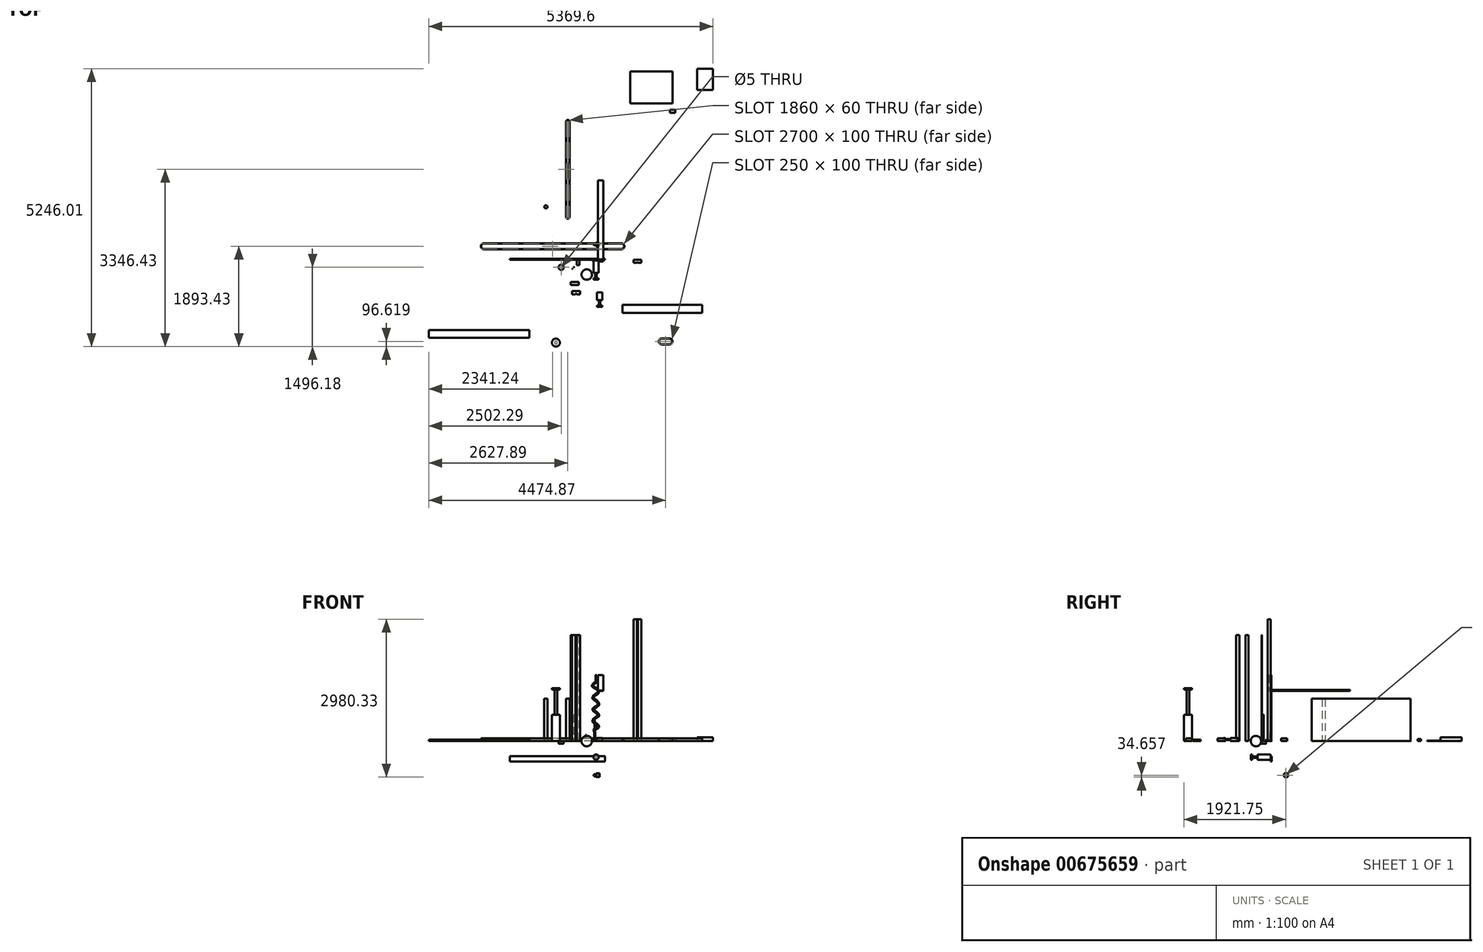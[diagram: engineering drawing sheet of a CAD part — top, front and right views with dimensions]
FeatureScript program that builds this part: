
annotation { "Feature Type Name" : "Feature", "Feature Type Description" : "" }
export const myFeature = defineFeature(function(context is Context, id is Id, definition is map)
    precondition{}
    {
        {
            var Q0;
            Q0=qCreatedBy(makeId("Top.planeOp"),FACE);
            var sketch = newSketch(context, id + "F0", { "sketchPlane" : qUnion([Q0])});
            skCircle(sketch, "E0", {"center": v(-422.62, -169.33) * mm, "radius": 2.5 * mm});
            skSolve(sketch);
        }
        {
            var Q0;
            Q0=makeQuery(id+"F0.imprint","IMPRINT",FACE,{"disambiguationData":[TD([[makeQuery(id+"F0.imprint","IMPRINT",EDGE,{"derivedFrom":sQuery(id+"F0.wireOp",EDGE,"E0")}),1.0]])]});
            extrude(context, id + "F1", {"entities" : qUnion([Q0]), "depth" : 2000 * mm, "offsetDistance" : 25 * mm});
        }
        {
            var Q0;
            Q0=qCreatedBy(makeId("Top.planeOp"),FACE);
            var sketch = newSketch(context, id + "F2", { "sketchPlane" : qUnion([Q0])});
            skCircle(sketch, "E1", {"center": v(-634.46, -142.18) * mm, "radius": 50 * mm});
            skCircle(sketch, "E2", {"center": v(-634.46, -142.18) * mm, "radius": 2.5 * mm});
            skSolve(sketch);
        }
        {
            var Q0;
            Q0=makeQuery(id+"F2.imprint","IMPRINT",FACE,{"disambiguationData":[TD([[makeQuery(id+"F2.imprint","IMPRINT",EDGE,{"derivedFrom":sQuery(id+"F2.wireOp",EDGE,"E1")}),1.0]])]});
            extrude(context, id + "F3", {"entities" : qUnion([Q0]), "oppositeDirection" : true, "depth" : 50 * mm, "offsetDistance" : 25 * mm});
        }
        {
            var Q0;
            Q0=qCreatedBy(makeId("Top.planeOp"),FACE);
            var sketch = newSketch(context, id + "F4", { "sketchPlane" : qUnion([Q0])});
            skLineSegment(sketch, "E3", {"start": v(-97.3, -196.52) * mm, "end": v(-205.2, -361.27) * mm, "construction": true});
            skArc(sketch, "E4", {"start": v(-205.2, -361.27) * mm, "mid": v(-68.88, -332.84) * mm, "end": v(-97.3, -196.52) * mm});
            skLineSegment(sketch, "E5", {"start": v(-205.2, -361.27) * mm, "end": v(-97.3, -196.52) * mm});
            skSolve(sketch);
        }
        {
            var Q0;
            Q0=makeQuery(id+"F4.imprint","IMPRINT",FACE,{"disambiguationData":[TD([[makeQuery(id+"F4.imprint","IMPRINT",EDGE,{"derivedFrom":sQuery(id+"F4.wireOp",EDGE,"E4")}),1.0]])]});
            var Q1;
            Q1=sQuery(id+"F4.wireOp",EDGE,"E4");
            var Q2;
            Q2=sQuery(id+"F4.wireOp",EDGE,"E5");
            revolve(context, id + "F5", {"entities" : qUnion([Q0]), "surfaceEntities" : qUnion([Q1]), "axis" : qUnion([Q2]), "revolveType" : RevolveType.FULL});
        }
        {
            var Q0;
            Q0=qCreatedBy(makeId("Top.planeOp"),FACE);
            var sketch = newSketch(context, id + "F6", { "sketchPlane" : qUnion([Q0])});
            skLineSegment(sketch, "E6.bottom", {"start": v(-2095.5, 305.07) * mm, "end": v(504.5, 305.07) * mm});
            skLineSegment(sketch, "E6.top", {"start": v(-2095.5, 205.07) * mm, "end": v(504.5, 205.07) * mm});
            skArc(sketch, "E7", {"start": v(504.5, 205.07) * mm, "mid": v(554.5, 255.07) * mm, "end": v(504.5, 305.07) * mm});
            skArc(sketch, "E8", {"start": v(-2095.5, 305.07) * mm, "mid": v(-2145.5, 255.07) * mm, "end": v(-2095.5, 205.07) * mm});
            skLineSegment(sketch, "E9.bottom", {"start": v(504.5, 311.07) * mm, "end": v(-2095.5, 311.07) * mm});
            skLineSegment(sketch, "E9.top", {"start": v(504.5, 199.07) * mm, "end": v(-2095.5, 199.07) * mm});
            skLineSegment(sketch, "E9.left", {"start": v(504.5, 311.07) * mm, "end": v(504.5, 199.07) * mm});
            skLineSegment(sketch, "E9.right", {"start": v(-2095.5, 311.07) * mm, "end": v(-2095.5, 199.07) * mm});
            skPoint(sketch, "E9.middle", {"position": v(-795.5, 255.07) * mm});
            skPoint(sketch, "E9.middle.positionSnap0", {"position": v(-795.5, 205.07) * mm});
            skPoint(sketch, "E9.centerSnap0", {"position": v(-795.5, 205.07) * mm});
            skArc(sketch, "E10", {"start": v(504.5, 199.07) * mm, "mid": v(560.5, 255.07) * mm, "end": v(504.5, 311.07) * mm});
            skArc(sketch, "E11", {"start": v(-2095.5, 311.07) * mm, "mid": v(-2151.5, 255.07) * mm, "end": v(-2095.5, 199.07) * mm});
            skSolve(sketch);
        }
        {
            var Q0;
            {var subQ0=sQuery(id+"F6.wireOp",EDGE,"E6.top");Q0=makeQuery(id+"F6.imprint","IMPRINT",FACE,{"disambiguationData":[TD([[makeQuery(id+"F6.imprint","IMPRINT",EDGE,{"derivedFrom":subQ0}),-1.0]])]});}
            var Q1;
            {var subQ0=sQuery(id+"F6.wireOp",EDGE,"E8");Q1=makeQuery(id+"F6.imprint","IMPRINT",FACE,{"disambiguationData":[TD([[makeQuery(id+"F6.imprint","IMPRINT",EDGE,{"derivedFrom":subQ0}),-1.0]])]});}
            var Q2;
            {var subQ0=sQuery(id+"F6.wireOp",EDGE,"E6.bottom");Q2=makeQuery(id+"F6.imprint","IMPRINT",FACE,{"disambiguationData":[TD([[makeQuery(id+"F6.imprint","IMPRINT",EDGE,{"derivedFrom":subQ0}),1.0]])]});}
            var Q3;
            {var subQ0=sQuery(id+"F6.wireOp",EDGE,"E7");Q3=makeQuery(id+"F6.imprint","IMPRINT",FACE,{"disambiguationData":[TD([[makeQuery(id+"F6.imprint","IMPRINT",EDGE,{"derivedFrom":subQ0}),-1.0]])]});}
            extrude(context, id + "F7", {"entities" : qUnion([Q0, Q1, Q2, Q3]), "depth" : 50 * mm, "offsetDistance" : 25 * mm});
        }
        {
            var Q0;
            Q0=qCreatedBy(makeId("Front.planeOp"),FACE);
            var sketch = newSketch(context, id + "F8", { "sketchPlane" : qUnion([Q0])});
            skLineSegment(sketch, "E12.bottom", {"start": v(-172.22, 116.45) * mm, "end": v(-157.22, 116.45) * mm});
            skLineSegment(sketch, "E12.top", {"start": v(-172.22, 56.45) * mm, "end": v(-157.22, 56.45) * mm});
            skLineSegment(sketch, "E12.left", {"start": v(-172.22, 116.45) * mm, "end": v(-172.22, 56.45) * mm});
            skLineSegment(sketch, "E12.right", {"start": v(-157.22, 116.45) * mm, "end": v(-157.22, 56.45) * mm});
            skSolve(sketch);
        }
        {
            var Q0;
            Q0=makeQuery(id+"F8.imprint","IMPRINT",FACE,{"disambiguationData":[TD([[makeQuery(id+"F8.imprint","IMPRINT",EDGE,{"derivedFrom":sQuery(id+"F8.wireOp",EDGE,"E12.bottom")}),-1.0]])]});
            extrude(context, id + "F9", {"entities" : qUnion([Q0]), "oppositeDirection" : true, "depth" : 15 * mm, "offsetDistance" : 25 * mm});
        }
        {
            var Q0;
            Q0=qCreatedBy(makeId("Front.planeOp"),FACE);
            var sketch = newSketch(context, id + "F10", { "sketchPlane" : qUnion([Q0])});
            skLineSegment(sketch, "E13.bottom", {"start": v(195.89, -284.97) * mm, "end": v(-1604.11, -284.97) * mm});
            skLineSegment(sketch, "E13.top", {"start": v(195.89, -384.97) * mm, "end": v(-1604.11, -384.97) * mm});
            skLineSegment(sketch, "E13.left", {"start": v(195.89, -284.97) * mm, "end": v(195.89, -384.97) * mm});
            skLineSegment(sketch, "E13.right", {"start": v(-1604.11, -284.97) * mm, "end": v(-1604.11, -384.97) * mm});
            skSolve(sketch);
        }
        {
            var Q0;
            Q0=makeQuery(id+"F10.imprint","IMPRINT",FACE,{"disambiguationData":[TD([[makeQuery(id+"F10.imprint","IMPRINT",EDGE,{"derivedFrom":sQuery(id+"F10.wireOp",EDGE,"E13.bottom")}),1.0]])]});
            extrude(context, id + "F11", {"entities" : qUnion([Q0]), "oppositeDirection" : true, "depth" : 20 * mm, "offsetDistance" : 25 * mm});
        }
        {
            var Q0;
            Q0=qCreatedBy(makeId("Front.planeOp"),FACE);
            var sketch = newSketch(context, id + "F12", { "sketchPlane" : qUnion([Q0])});
            skLineSegment(sketch, "E14.bottom", {"start": v(162.63, 1244.6) * mm, "end": v(62.63, 1244.6) * mm});
            skLineSegment(sketch, "E14.top", {"start": v(162.63, 944.6) * mm, "end": v(62.63, 944.6) * mm});
            skLineSegment(sketch, "E14.left", {"start": v(162.63, 1244.6) * mm, "end": v(162.63, 944.6) * mm});
            skLineSegment(sketch, "E14.right", {"start": v(62.63, 1244.6) * mm, "end": v(62.63, 944.6) * mm});
            skSolve(sketch);
        }
        {
            var Q0;
            Q0=makeQuery(id+"F12.imprint","IMPRINT",FACE,{"disambiguationData":[TD([[makeQuery(id+"F12.imprint","IMPRINT",EDGE,{"derivedFrom":sQuery(id+"F12.wireOp",EDGE,"E14.bottom")}),1.0]])]});
            var Q1;
            Q1=makeQuery(id+"F12.imprint","IMPRINT",FACE,{"disambiguationData":[TD([[makeQuery(id+"F12.imprint","IMPRINT",EDGE,{"derivedFrom":sQuery(id+"F12.wireOp",EDGE,"OlUaidlP-VtYr-vpI1-CS2M-X3MWIcY6ebwZ.bottom")}),-1.0]])]});
            extrude(context, id + "F13", {"entities" : qUnion([Q0, Q1]), "depth" : 30 * mm, "offsetDistance" : 25 * mm});
        }
        {
            var Q0;
            Q0=makeQuery(id+"F13.opExtrude","CAP_FACE",FACE,{"disambiguationData":[OSD([sQuery(id+"F12.wireOp",EDGE,"E14.bottom"),sQuery(id+"F12.wireOp",EDGE,"E14.top"),sQuery(id+"F12.wireOp",EDGE,"E14.left"),sQuery(id+"F12.wireOp",EDGE,"E14.right")])],"isStart":true});
            var sketch = newSketch(context, id + "F14", { "sketchPlane" : qUnion([Q0])});
            skLineSegment(sketch, "E15.bottom", {"start": v(-162.63, 944.6) * mm, "end": v(-62.63, 944.6) * mm});
            skLineSegment(sketch, "E15.top", {"start": v(-162.63, 964.6) * mm, "end": v(-62.63, 964.6) * mm});
            skLineSegment(sketch, "E15.left", {"start": v(-162.63, 944.6) * mm, "end": v(-162.63, 964.6) * mm});
            skLineSegment(sketch, "E15.right", {"start": v(-62.63, 944.6) * mm, "end": v(-62.63, 964.6) * mm});
            skSolve(sketch);
        }
        {
            var Q0;
            Q0=makeQuery(id+"F14.imprint","IMPRINT",FACE,{"disambiguationData":[TD([[makeQuery(id+"F14.imprint","IMPRINT",EDGE,{"derivedFrom":sQuery(id+"F14.wireOp",EDGE,"E15.bottom")}),1.0]])]});
            extrude(context, id + "F15", {"entities" : qUnion([Q0]), "operationType" : NewBodyOperationType.ADD, "depth" : 1500 * mm, "offsetDistance" : 25 * mm});
        }
        {
            var Q0;
            Q0=qCreatedBy(makeId("Top.planeOp"),FACE);
            var sketch = newSketch(context, id + "F16", { "sketchPlane" : qUnion([Q0])});
            skCircle(sketch, "E16", {"center": v(-392.08, -137.9) * mm, "radius": 2.5 * mm});
            skSolve(sketch);
        }
        {
            var Q0;
            Q0=makeQuery(id+"F16.imprint","IMPRINT",FACE,{"disambiguationData":[TD([[makeQuery(id+"F16.imprint","IMPRINT",EDGE,{"derivedFrom":sQuery(id+"F16.wireOp",EDGE,"E16")}),1.0]])]});
            extrude(context, id + "F17", {"entities" : qUnion([Q0]), "depth" : 500 * mm, "offsetDistance" : 25 * mm});
        }
        {
            var Q0;
            Q0=qCreatedBy(makeId("Top.planeOp"),FACE);
            var sketch = newSketch(context, id + "F18", { "sketchPlane" : qUnion([Q0])});
            skLineSegment(sketch, "E17.bottom", {"start": v(1263.12, -1491.74) * mm, "end": v(1413.12, -1491.74) * mm});
            skLineSegment(sketch, "E17.top", {"start": v(1263.12, -1591.74) * mm, "end": v(1413.12, -1591.74) * mm});
            skArc(sketch, "E18", {"start": v(1413.12, -1591.74) * mm, "mid": v(1463.12, -1541.74) * mm, "end": v(1413.12, -1491.74) * mm});
            skArc(sketch, "E19", {"start": v(1263.12, -1491.74) * mm, "mid": v(1213.12, -1541.74) * mm, "end": v(1263.12, -1591.74) * mm});
            skLineSegment(sketch, "E20.bottom", {"start": v(1413.12, -1485.74) * mm, "end": v(1263.12, -1485.74) * mm});
            skLineSegment(sketch, "E20.top", {"start": v(1413.12, -1597.74) * mm, "end": v(1263.12, -1597.74) * mm});
            skLineSegment(sketch, "E20.left", {"start": v(1413.12, -1485.74) * mm, "end": v(1413.12, -1597.74) * mm});
            skLineSegment(sketch, "E20.right", {"start": v(1263.12, -1485.74) * mm, "end": v(1263.12, -1597.74) * mm});
            skPoint(sketch, "E20.middle", {"position": v(1338.12, -1541.74) * mm});
            skPoint(sketch, "E20.middle.positionSnap0", {"position": v(1338.12, -1591.74) * mm});
            skPoint(sketch, "E20.centerSnap0", {"position": v(1338.12, -1591.74) * mm});
            skArc(sketch, "E21", {"start": v(1413.12, -1597.74) * mm, "mid": v(1469.12, -1541.74) * mm, "end": v(1413.12, -1485.74) * mm});
            skArc(sketch, "E22", {"start": v(1263.12, -1485.74) * mm, "mid": v(1207.12, -1541.74) * mm, "end": v(1263.12, -1597.74) * mm});
            skSolve(sketch);
        }
        {
            var Q0;
            {var subQ0=sQuery(id+"F18.wireOp",EDGE,"E17.top");Q0=makeQuery(id+"F18.imprint","IMPRINT",FACE,{"disambiguationData":[TD([[makeQuery(id+"F18.imprint","IMPRINT",EDGE,{"derivedFrom":subQ0}),-1.0]])]});}
            var Q1;
            {var subQ0=sQuery(id+"F18.wireOp",EDGE,"E19");Q1=makeQuery(id+"F18.imprint","IMPRINT",FACE,{"disambiguationData":[TD([[makeQuery(id+"F18.imprint","IMPRINT",EDGE,{"derivedFrom":subQ0}),-1.0]])]});}
            var Q2;
            {var subQ0=sQuery(id+"F18.wireOp",EDGE,"E17.bottom");Q2=makeQuery(id+"F18.imprint","IMPRINT",FACE,{"disambiguationData":[TD([[makeQuery(id+"F18.imprint","IMPRINT",EDGE,{"derivedFrom":subQ0}),1.0]])]});}
            var Q3;
            {var subQ0=sQuery(id+"F18.wireOp",EDGE,"E18");Q3=makeQuery(id+"F18.imprint","IMPRINT",FACE,{"disambiguationData":[TD([[makeQuery(id+"F18.imprint","IMPRINT",EDGE,{"derivedFrom":subQ0}),-1.0]])]});}
            extrude(context, id + "F19", {"entities" : qUnion([Q0, Q1, Q2, Q3]), "depth" : 50 * mm, "offsetDistance" : 25 * mm});
        }
        {
            var Q0;
            Q0=qCreatedBy(makeId("Top.planeOp"),FACE);
            var sketch = newSketch(context, id + "F20", { "sketchPlane" : qUnion([Q0])});
            skLineSegment(sketch, "E23.bottom", {"start": v(143.97, -613.5) * mm, "end": v(43.97, -613.5) * mm});
            skLineSegment(sketch, "E23.top", {"start": v(143.97, -763.5) * mm, "end": v(43.97, -763.5) * mm});
            skLineSegment(sketch, "E23.left", {"start": v(143.97, -613.5) * mm, "end": v(143.97, -763.5) * mm});
            skLineSegment(sketch, "E23.right", {"start": v(43.97, -613.5) * mm, "end": v(43.97, -763.5) * mm});
            skSolve(sketch);
        }
        {
            var Q0;
            Q0=makeQuery(id+"F20.imprint","IMPRINT",FACE,{"disambiguationData":[TD([[makeQuery(id+"F20.imprint","IMPRINT",EDGE,{"derivedFrom":sQuery(id+"F20.wireOp",EDGE,"E23.bottom")}),1.0]])]});
            extrude(context, id + "F21", {"entities" : qUnion([Q0]), "depth" : 60 * mm, "offsetDistance" : 25 * mm});
        }
        {
            var Q0;
            Q0=makeQuery(id+"F21.opExtrude","SWEPT_FACE",FACE,{"disambiguationData":[OSD([sQuery(id+"F20.wireOp",EDGE,"E23.top")])]});
            var sketch = newSketch(context, id + "F22", { "sketchPlane" : qUnion([Q0])});
            skCircle(sketch, "E24", {"center": v(93.97, 30) * mm, "radius": 12.5 * mm});
            skPoint(sketch, "E24.centerSnap0", {"position": v(93.97, 0) * mm});
            skPoint(sketch, "E24.centerSnap1", {"position": v(143.97, 30) * mm});
            skSolve(sketch);
        }
        {
            var Q0;
            Q0=makeQuery(id+"F22.imprint","IMPRINT",FACE,{"disambiguationData":[TD([[makeQuery(id+"F22.imprint","IMPRINT",EDGE,{"derivedFrom":sQuery(id+"F22.wireOp",EDGE,"E24")}),1.0]])]});
            extrude(context, id + "F23", {"entities" : qUnion([Q0]), "operationType" : NewBodyOperationType.ADD, "depth" : 100 * mm, "offsetDistance" : 25 * mm});
        }
        {
            var Q0;
            Q0=makeQuery(id+"F23.opExtrude","CAP_FACE",FACE,{"disambiguationData":[OSD([sQuery(id+"F22.wireOp",EDGE,"E24")])],"isStart":false});
            var sketch = newSketch(context, id + "F24", { "sketchPlane" : qUnion([Q0])});
            skLineSegment(sketch, "E25.bottom", {"start": v(43.97, 60) * mm, "end": v(143.97, 60) * mm});
            skLineSegment(sketch, "E25.top", {"start": v(43.97, 0) * mm, "end": v(143.97, 0) * mm});
            skLineSegment(sketch, "E25.left", {"start": v(43.97, 60) * mm, "end": v(43.97, 0) * mm});
            skLineSegment(sketch, "E25.right", {"start": v(143.97, 60) * mm, "end": v(143.97, 0) * mm});
            skPoint(sketch, "E25.middle", {"position": v(93.97, 30) * mm});
            skSolve(sketch);
        }
        {
            var Q0;
            Q0=makeQuery(id+"F24.imprint","IMPRINT",FACE,{"disambiguationData":[TD([[makeQuery(id+"F24.imprint","IMPRINT",EDGE,{"derivedFrom":makeQuery(id+"F23.opExtrude","CAP_EDGE",EDGE,{"disambiguationData":[OSD([sQuery(id+"F22.wireOp",EDGE,"E24")])],"isStart":false})}),1.0]])]});
            var Q1;
            Q1=makeQuery(id+"F24.imprint","IMPRINT",FACE,{"disambiguationData":[TD([[makeQuery(id+"F24.imprint","IMPRINT",EDGE,{"derivedFrom":sQuery(id+"F24.wireOp",EDGE,"E25.bottom")}),-1.0]])]});
            extrude(context, id + "F25", {"entities" : qUnion([Q0, Q1]), "operationType" : NewBodyOperationType.ADD, "depth" : 25 * mm, "offsetDistance" : 25 * mm});
        }
        {
            var Q0;
            Q0=qCreatedBy(makeId("Front.planeOp"),FACE);
            var sketch = newSketch(context, id + "F26", { "sketchPlane" : qUnion([Q0])});
            skFitSpline(sketch, "E26", {"points": [v(0, 51) * mm, v(-5.84, 62.76) * mm, v(0, 70.71) * mm, v(4.67, 77.84) * mm, v(0, 83.94) * mm, v(-5.26, 93.35) * mm, v(0, 101.45) * mm, v(4.37, 108.33) * mm, v(0, 116.03) * mm, v(-4.74, 124.5) * mm, v(0, 133.6) * mm, v(3.8, 139.5) * mm, v(0, 146.22) * mm, v(-4.93, 154.09) * mm, v(0, 161.1) * mm, v(3.78, 166.85) * mm, v(0, 171.88) * mm, v(-4.67, 179.78) * mm, v(0, 187.27) * mm, v(4.37, 192.98) * mm, v(0, 199.35) * mm, v(-4.63, 204.84) * mm, v(1.46, 214.13) * mm], "startDerivative": vector(-175.87, 321.08) * mm, "endDerivative": vector(259.3, 263.4) * mm});
            skFitSpline(sketch, "E27", {"points": [v(1.46, 214.13) * mm, v(-4, 229.18) * mm, v(-2, 237.03) * mm, v(3.59, 245.52) * mm, v(-1.97, 252.6) * mm, v(-5.26, 256.84) * mm, v(0, 264.93) * mm, v(4.37, 271.82) * mm, v(0, 279.51) * mm, v(-4.74, 287.99) * mm, v(0, 297.09) * mm, v(3.8, 303) * mm, v(0, 309.7) * mm, v(-4.93, 317.57) * mm, v(0, 324.58) * mm, v(3.78, 330.33) * mm, v(0, 335.37) * mm, v(-4.67, 343.27) * mm, v(0, 350.76) * mm, v(4.37, 356.46) * mm, v(0, 362.83) * mm, v(-4.63, 368.33) * mm, v(0, 377.97) * mm], "startDerivative": vector(407.97, 395.9) * mm, "endDerivative": vector(276.44, 125.82) * mm});
            skLineSegment(sketch, "E28", {"start": v(0, 51) * mm, "end": v(0, 0) * mm});
            skLineSegment(sketch, "E29", {"start": v(0, 377.97) * mm, "end": v(0, 390.56) * mm});
            skSolve(sketch);
        }
        {
            var Q0;
            Q0=qCreatedBy(makeId("Top.planeOp"),FACE);
            var sketch = newSketch(context, id + "F27", { "sketchPlane" : qUnion([Q0])});
            skCircle(sketch, "E30", {"center": v(0, 0) * mm, "radius": 2 * mm});
            skSolve(sketch);
        }
        {
            var Q0;
            Q0=makeQuery(id+"F27.imprint","IMPRINT",FACE,{"disambiguationData":[TD([[makeQuery(id+"F27.imprint","IMPRINT",EDGE,{"derivedFrom":sQuery(id+"F27.wireOp",EDGE,"E30")}),1.0]])]});
            var Q1;
            Q1=sQuery(id+"F26.wireOp",EDGE,"E28");
            var Q2;
            Q2=sQuery(id+"F26.wireOp",EDGE,"E26");
            var Q3;
            Q3=sQuery(id+"F26.wireOp",EDGE,"E27");
            var Q4;
            Q4=sQuery(id+"F26.wireOp",EDGE,"E29");
            sweep(context, id + "F28", {"profiles" : qUnion([Q0]), "path" : qUnion([Q1, Q2, Q3, Q4])});
        }
        {
            var Q0;
            Q0=makeQuery(id+"F9.opExtrude","SWEPT_FACE",FACE,{"disambiguationData":[OSD([sQuery(id+"F8.wireOp",EDGE,"E12.top")])]});
            var sketch = newSketch(context, id + "F29", { "sketchPlane" : qUnion([Q0])});
            skCircle(sketch, "E31", {"center": v(-157.22, -7.5) * mm, "radius": 2.5 * mm});
            skSolve(sketch);
        }
        {
            var Q0;
            {var subQ0=sQuery(id+"F29.wireOp",EDGE,"E31");var subQ1=makeQuery(id+"F9.opExtrude","SWEPT_EDGE",EDGE,{"disambiguationData":[OSD([sQuery(id+"F8.wireOp",EDGE,"E12.top"),sQuery(id+"F8.wireOp",EDGE,"E12.right")])]});var subQ2=makeQuery(id+"F29.imprint","INTERSECT",VERTEX,{"disambiguationData":[OD(0.0)],"derivedFrom":[subQ1,subQ0]});Q0=makeQuery(id+"F29.imprint","IMPRINT",FACE,{"disambiguationData":[TD([[makeQuery(id+"F29.imprint","IMPRINT",EDGE,{"disambiguationData":[TD([[subQ2,-1.0]])],"derivedFrom":subQ0}),1.0]])]});}
            extrude(context, id + "F30", {"entities" : qUnion([Q0]), "operationType" : NewBodyOperationType.REMOVE, "endBound" : BoundingType.UP_TO_NEXT, "oppositeDirection" : true, "depth" : 25 * mm, "offsetDistance" : 25 * mm});
        }
        {
            var Q0;
            Q0=qCreatedBy(makeId("Right.planeOp"),FACE);
            var sketch = newSketch(context, id + "F31", { "sketchPlane" : qUnion([Q0])});
            skLineSegment(sketch, "E32", {"start": v(284.89, -626.13) * mm, "end": v(296.14, -664.52) * mm});
            skArc(sketch, "E33", {"start": v(284.89, -626.13) * mm, "mid": v(271.32, -650.95) * mm, "end": v(296.14, -664.52) * mm});
            skCircle(sketch, "E34", {"center": v(290.51, -645.33) * mm, "radius": 10 * mm});
            skSolve(sketch);
        }
        {
            var Q0;
            Q0=makeQuery(id+"F31.imprint","IMPRINT",FACE,{"disambiguationData":[TD([[makeQuery(id+"F31.imprint","IMPRINT",EDGE,{"derivedFrom":sQuery(id+"F31.wireOp",EDGE,"E32")}),-1.0]])]});
            var Q1;
            Q1=sQuery(id+"F31.wireOp",EDGE,"E32");
            revolve(context, id + "F32", {"entities" : qUnion([Q0]), "axis" : qUnion([Q1]), "revolveType" : RevolveType.FULL});
        }
        {
            var Q0;
            {var subQ0=sQuery(id+"F31.wireOp",EDGE,"E34");var subQ1=sQuery(id+"F31.wireOp",EDGE,"E32");var subQ2=makeQuery(id+"F31.imprint","INTERSECT",VERTEX,{"disambiguationData":[OD(0.0)],"derivedFrom":[subQ1,subQ0]});Q0=makeQuery(id+"F31.imprint","IMPRINT",FACE,{"disambiguationData":[TD([[makeQuery(id+"F31.imprint","IMPRINT",EDGE,{"disambiguationData":[TD([[subQ2,-1.0]])],"derivedFrom":subQ1}),1.0]])]});}
            var Q1;
            {var subQ0=sQuery(id+"F31.wireOp",EDGE,"E34");var subQ1=sQuery(id+"F31.wireOp",EDGE,"E32");var subQ2=makeQuery(id+"F31.imprint","INTERSECT",VERTEX,{"disambiguationData":[OD(0.0)],"derivedFrom":[subQ1,subQ0]});Q1=makeQuery(id+"F31.imprint","IMPRINT",FACE,{"disambiguationData":[TD([[makeQuery(id+"F31.imprint","IMPRINT",EDGE,{"disambiguationData":[TD([[subQ2,-1.0]])],"derivedFrom":subQ1}),-1.0]])]});}
            extrude(context, id + "F33", {"entities" : qUnion([Q0, Q1]), "operationType" : NewBodyOperationType.ADD, "depth" : 25 * mm, "offsetDistance" : 25 * mm});
        }
        {
            var Q0;
            Q0=makeQuery(id+"F33.opExtrude","CAP_FACE",FACE,{"disambiguationData":[OSD([sQuery(id+"F31.wireOp",EDGE,"E34")])],"isStart":false});
            var sketch = newSketch(context, id + "F34", { "sketchPlane" : qUnion([Q0])});
            skLineSegment(sketch, "E35.bottom", {"start": v(255.51, -680.33) * mm, "end": v(325.51, -680.33) * mm});
            skLineSegment(sketch, "E35.top", {"start": v(255.51, -610.33) * mm, "end": v(325.51, -610.33) * mm});
            skLineSegment(sketch, "E35.left", {"start": v(255.51, -680.33) * mm, "end": v(255.51, -610.33) * mm});
            skLineSegment(sketch, "E35.right", {"start": v(325.51, -680.33) * mm, "end": v(325.51, -610.33) * mm});
            skPoint(sketch, "E35.middle", {"position": v(290.51, -645.33) * mm});
            skSolve(sketch);
        }
        {
            var Q0;
            Q0=makeQuery(id+"F34.imprint","IMPRINT",FACE,{"disambiguationData":[TD([[makeQuery(id+"F34.imprint","IMPRINT",EDGE,{"derivedFrom":sQuery(id+"F34.wireOp",EDGE,"E35.bottom")}),1.0]])]});
            var Q1;
            Q1=makeQuery(id+"F34.imprint","IMPRINT",FACE,{"disambiguationData":[TD([[makeQuery(id+"F34.imprint","IMPRINT",EDGE,{"derivedFrom":makeQuery(id+"F33.opExtrude","CAP_EDGE",EDGE,{"disambiguationData":[OSD([sQuery(id+"F31.wireOp",EDGE,"E34")])],"isStart":false})}),1.0]])]});
            extrude(context, id + "F35", {"entities" : qUnion([Q0, Q1]), "operationType" : NewBodyOperationType.ADD, "depth" : 70 * mm, "offsetDistance" : 25 * mm});
        }
        {
            var Q0;
            Q0=qCreatedBy(makeId("Front.planeOp"),FACE);
            var sketch = newSketch(context, id + "F36", { "sketchPlane" : qUnion([Q0])});
            skCircle(sketch, "E36", {"center": v(25.1, -302.8) * mm, "radius": 50 * mm});
            skSolve(sketch);
        }
        {
            var Q0;
            Q0=makeQuery(id+"F36.imprint","IMPRINT",FACE,{"disambiguationData":[TD([[makeQuery(id+"F36.imprint","IMPRINT",EDGE,{"derivedFrom":sQuery(id+"F36.wireOp",EDGE,"E36")}),1.0]])]});
            extrude(context, id + "F37", {"entities" : qUnion([Q0]), "depth" : 250 * mm, "offsetDistance" : 25 * mm});
        }
        {
            var Q0;
            Q0=makeQuery(id+"F37.opExtrude","CAP_FACE",FACE,{"disambiguationData":[OSD([sQuery(id+"F36.wireOp",EDGE,"E36")])],"isStart":false});
            var sketch = newSketch(context, id + "F38", { "sketchPlane" : qUnion([Q0])});
            skCircle(sketch, "E37", {"center": v(25.1, -302.8) * mm, "radius": 12.5 * mm});
            skSolve(sketch);
        }
        {
            var Q0;
            Q0=makeQuery(id+"F38.imprint","IMPRINT",FACE,{"disambiguationData":[TD([[makeQuery(id+"F38.imprint","IMPRINT",EDGE,{"derivedFrom":sQuery(id+"F38.wireOp",EDGE,"E37")}),1.0]])]});
            extrude(context, id + "F39", {"entities" : qUnion([Q0]), "operationType" : NewBodyOperationType.ADD, "depth" : 100 * mm, "offsetDistance" : 25 * mm});
        }
        {
            var Q0;
            Q0=makeQuery(id+"F39.opExtrude","CAP_FACE",FACE,{"disambiguationData":[OSD([sQuery(id+"F38.wireOp",EDGE,"E37")])],"isStart":false});
            var sketch = newSketch(context, id + "F40", { "sketchPlane" : qUnion([Q0])});
            skCircle(sketch, "E38", {"center": v(25.1, -302.8) * mm, "radius": 50 * mm});
            skSolve(sketch);
        }
        {
            var Q0;
            Q0=makeQuery(id+"F40.imprint","IMPRINT",FACE,{"disambiguationData":[TD([[makeQuery(id+"F40.imprint","IMPRINT",EDGE,{"derivedFrom":sQuery(id+"F40.wireOp",EDGE,"E38")}),1.0]])]});
            var Q1;
            Q1=makeQuery(id+"F40.imprint","IMPRINT",FACE,{"disambiguationData":[TD([[makeQuery(id+"F40.imprint","IMPRINT",EDGE,{"derivedFrom":makeQuery(id+"F39.opExtrude","CAP_EDGE",EDGE,{"disambiguationData":[OSD([sQuery(id+"F38.wireOp",EDGE,"E37")])],"isStart":false})}),1.0]])]});
            extrude(context, id + "F41", {"entities" : qUnion([Q0, Q1]), "operationType" : NewBodyOperationType.ADD, "depth" : 25 * mm, "offsetDistance" : 25 * mm});
        }
        {
            var Q0;
            Q0=qCreatedBy(makeId("Top.planeOp"),FACE);
            var sketch = newSketch(context, id + "F42", { "sketchPlane" : qUnion([Q0])});
            skLineSegment(sketch, "E39.bottom", {"start": v(-338.4, 0) * mm, "end": v(-288.4, 0) * mm});
            skLineSegment(sketch, "E39.top", {"start": v(-338.4, -100) * mm, "end": v(-288.4, -100) * mm});
            skLineSegment(sketch, "E39.left", {"start": v(-338.4, 0) * mm, "end": v(-338.4, -100) * mm});
            skLineSegment(sketch, "E39.right", {"start": v(-288.4, 0) * mm, "end": v(-288.4, -100) * mm});
            skSolve(sketch);
        }
        {
            var Q0;
            Q0=makeQuery(id+"F42.imprint","IMPRINT",FACE,{"disambiguationData":[TD([[makeQuery(id+"F42.imprint","IMPRINT",EDGE,{"derivedFrom":sQuery(id+"F42.wireOp",EDGE,"E39.bottom")}),-1.0]])]});
            extrude(context, id + "F43", {"entities" : qUnion([Q0]), "depth" : 20 * mm, "offsetDistance" : 25 * mm});
        }
        {
            var Q0;
            Q0=qCreatedBy(makeId("Top.planeOp"),FACE);
            var sketch = newSketch(context, id + "F44", { "sketchPlane" : qUnion([Q0])});
            skLineSegment(sketch, "E40.bottom", {"start": v(-3136.75, -1323.94) * mm, "end": v(-1236.75, -1323.94) * mm});
            skLineSegment(sketch, "E40.top", {"start": v(-3136.75, -1473.94) * mm, "end": v(-1236.75, -1473.94) * mm});
            skLineSegment(sketch, "E40.left", {"start": v(-3136.75, -1323.94) * mm, "end": v(-3136.75, -1473.94) * mm});
            skLineSegment(sketch, "E40.right", {"start": v(-1236.75, -1323.94) * mm, "end": v(-1236.75, -1473.94) * mm});
            skSolve(sketch);
        }
        {
            var Q0;
            Q0=makeQuery(id+"F44.imprint","IMPRINT",FACE,{"disambiguationData":[TD([[makeQuery(id+"F44.imprint","IMPRINT",EDGE,{"derivedFrom":sQuery(id+"F44.wireOp",EDGE,"E40.bottom")}),-1.0]])]});
            extrude(context, id + "F45", {"entities" : qUnion([Q0]), "depth" : 25 * mm, "offsetDistance" : 25 * mm});
        }
        {
            var Q0;
            Q0=qCreatedBy(makeId("Top.planeOp"),FACE);
            var sketch = newSketch(context, id + "F46", { "sketchPlane" : qUnion([Q0])});
            skCircle(sketch, "E41", {"center": v(-733.64, -1563.36) * mm, "radius": 75 * mm});
            skSolve(sketch);
        }
        {
            var Q0;
            Q0=makeQuery(id+"F46.imprint","IMPRINT",FACE,{"disambiguationData":[TD([[makeQuery(id+"F46.imprint","IMPRINT",EDGE,{"derivedFrom":sQuery(id+"F46.wireOp",EDGE,"E41")}),1.0]])]});
            extrude(context, id + "F47", {"entities" : qUnion([Q0]), "depth" : 500 * mm, "offsetDistance" : 25 * mm});
        }
        {
            var Q0;
            Q0=makeQuery(id+"F47.opExtrude","CAP_FACE",FACE,{"disambiguationData":[OSD([sQuery(id+"F46.wireOp",EDGE,"E41")])],"isStart":false});
            var sketch = newSketch(context, id + "F48", { "sketchPlane" : qUnion([Q0])});
            skCircle(sketch, "E42", {"center": v(-733.64, -1563.36) * mm, "radius": 25 * mm});
            skSolve(sketch);
        }
        {
            var Q0;
            Q0=makeQuery(id+"F48.imprint","IMPRINT",FACE,{"disambiguationData":[TD([[makeQuery(id+"F48.imprint","IMPRINT",EDGE,{"derivedFrom":sQuery(id+"F48.wireOp",EDGE,"E42")}),1.0]])]});
            extrude(context, id + "F49", {"entities" : qUnion([Q0]), "operationType" : NewBodyOperationType.ADD, "depth" : 470 * mm, "offsetDistance" : 25 * mm});
        }
        {
            var Q0;
            Q0=makeQuery(id+"F49.opExtrude","CAP_FACE",FACE,{"disambiguationData":[OSD([sQuery(id+"F48.wireOp",EDGE,"E42")])],"isStart":false});
            var sketch = newSketch(context, id + "F50", { "sketchPlane" : qUnion([Q0])});
            skCircle(sketch, "E43", {"center": v(-733.64, -1563.36) * mm, "radius": 75 * mm});
            skSolve(sketch);
        }
        {
            var Q0;
            Q0=makeQuery(id+"F50.imprint","IMPRINT",FACE,{"disambiguationData":[TD([[makeQuery(id+"F50.imprint","IMPRINT",EDGE,{"derivedFrom":sQuery(id+"F50.wireOp",EDGE,"E43")}),1.0]])]});
            var Q1;
            Q1=makeQuery(id+"F50.imprint","IMPRINT",FACE,{"disambiguationData":[TD([[makeQuery(id+"F50.imprint","IMPRINT",EDGE,{"derivedFrom":makeQuery(id+"F49.opExtrude","CAP_EDGE",EDGE,{"disambiguationData":[OSD([sQuery(id+"F48.wireOp",EDGE,"E42")])],"isStart":false})}),1.0]])]});
            extrude(context, id + "F51", {"entities" : qUnion([Q0, Q1]), "operationType" : NewBodyOperationType.ADD, "depth" : 30 * mm, "offsetDistance" : 25 * mm});
        }
        {
            var Q0;
            Q0=qCreatedBy(makeId("Top.planeOp"),FACE);
            var sketch = newSketch(context, id + "F52", { "sketchPlane" : qUnion([Q0])});
            skLineSegment(sketch, "E44.bottom", {"start": v(-453.69, -476.84) * mm, "end": v(-303.69, -476.84) * mm});
            skLineSegment(sketch, "E44.top", {"start": v(-453.69, -416.84) * mm, "end": v(-303.69, -416.84) * mm});
            skLineSegment(sketch, "E44.left", {"start": v(-453.69, -476.84) * mm, "end": v(-453.69, -416.84) * mm});
            skLineSegment(sketch, "E44.right", {"start": v(-303.69, -476.84) * mm, "end": v(-303.69, -416.84) * mm});
            skSolve(sketch);
        }
        {
            var Q0;
            Q0=makeQuery(id+"F52.imprint","IMPRINT",FACE,{"disambiguationData":[TD([[makeQuery(id+"F52.imprint","IMPRINT",EDGE,{"derivedFrom":sQuery(id+"F52.wireOp",EDGE,"E44.bottom")}),1.0]])]});
            extrude(context, id + "F53", {"entities" : qUnion([Q0]), "depth" : 2000 * mm, "offsetDistance" : 25 * mm});
        }
        {
            var Q0;
            Q0=qCreatedBy(makeId("Front.planeOp"),FACE);
            var sketch = newSketch(context, id + "F54", { "sketchPlane" : qUnion([Q0])});
            skFitSpline(sketch, "E45", {"points": [v(0, 167.64) * mm, v(-17.94, 208.61) * mm, v(73.51, 264.42) * mm, v(28.89, 322.37) * mm, v(-7.74, 344.4) * mm, v(-36.53, 386.12) * mm, v(24.83, 446.54) * mm, v(74.86, 488.26) * mm, v(17.96, 546.74) * mm, v(-35.29, 599.76) * mm, v(30.4, 654.41) * mm, v(75.62, 700.26) * mm, v(23.9, 762.77) * mm, v(-38.26, 816.58) * mm, v(24.05, 885.75) * mm, v(82.04, 935.65) * mm, v(23.63, 993.48) * mm, v(-40.54, 1048.05) * mm, v(27.16, 1117.7) * mm], "startDerivative": vector(-1301.07, 1065.42) * mm, "endDerivative": vector(1290.86, 893.97) * mm});
            skLineSegment(sketch, "E46", {"start": v(27.16, 1117.7) * mm, "end": v(27.16, 1244.6) * mm});
            skLineSegment(sketch, "E47", {"start": v(0, 167.64) * mm, "end": v(0, 0) * mm});
            skSolve(sketch);
        }
        {
            var Q0;
            Q0=qCreatedBy(makeId("Top.planeOp"),FACE);
            var sketch = newSketch(context, id + "F55", { "sketchPlane" : qUnion([Q0])});
            skCircle(sketch, "E48", {"center": v(0, 0) * mm, "radius": 12.5 * mm});
            skSolve(sketch);
        }
        {
            var Q0;
            Q0=makeQuery(id+"F55.imprint","IMPRINT",FACE,{"disambiguationData":[TD([[makeQuery(id+"F55.imprint","IMPRINT",EDGE,{"derivedFrom":sQuery(id+"F55.wireOp",EDGE,"E48")}),1.0]])]});
            var Q1;
            Q1=sQuery(id+"F54.wireOp",EDGE,"E47");
            var Q2;
            Q2=sQuery(id+"F54.wireOp",EDGE,"E45");
            var Q3;
            Q3=sQuery(id+"F54.wireOp",EDGE,"E46");
            sweep(context, id + "F56", {"profiles" : qUnion([Q0]), "path" : qUnion([Q1, Q2, Q3])});
        }
        {
            var Q0;
            Q0=qCreatedBy(makeId("Top.planeOp"),FACE);
            var sketch = newSketch(context, id + "F57", { "sketchPlane" : qUnion([Q0])});
            skLineSegment(sketch, "E49.bottom", {"start": v(526, -1001.95) * mm, "end": v(2026, -1001.95) * mm});
            skLineSegment(sketch, "E49.top", {"start": v(526, -851.95) * mm, "end": v(2026, -851.95) * mm});
            skLineSegment(sketch, "E49.left", {"start": v(526, -1001.95) * mm, "end": v(526, -851.95) * mm});
            skLineSegment(sketch, "E49.right", {"start": v(2026, -1001.95) * mm, "end": v(2026, -851.95) * mm});
            skSolve(sketch);
        }
        {
            var Q0;
            Q0=makeQuery(id+"F57.imprint","IMPRINT",FACE,{"disambiguationData":[TD([[makeQuery(id+"F57.imprint","IMPRINT",EDGE,{"derivedFrom":sQuery(id+"F57.wireOp",EDGE,"E49.bottom")}),1.0]])]});
            extrude(context, id + "F58", {"entities" : qUnion([Q0]), "depth" : 50 * mm, "offsetDistance" : 25 * mm});
        }
        {
            var Q0;
            Q0=qCreatedBy(makeId("Top.planeOp"),FACE);
            var sketch = newSketch(context, id + "F59", { "sketchPlane" : qUnion([Q0])});
            skLineSegment(sketch, "E50.bottom", {"start": v(-427.58, -651.93) * mm, "end": v(-277.58, -651.93) * mm});
            skLineSegment(sketch, "E50.top", {"start": v(-427.58, -591.93) * mm, "end": v(-277.58, -591.93) * mm});
            skLineSegment(sketch, "E50.left", {"start": v(-427.58, -651.93) * mm, "end": v(-427.58, -591.93) * mm});
            skLineSegment(sketch, "E50.right", {"start": v(-277.58, -651.93) * mm, "end": v(-277.58, -591.93) * mm});
            skSolve(sketch);
        }
        {
            var Q0;
            Q0=makeQuery(id+"F59.imprint","IMPRINT",FACE,{"disambiguationData":[TD([[makeQuery(id+"F59.imprint","IMPRINT",EDGE,{"derivedFrom":sQuery(id+"F59.wireOp",EDGE,"E50.bottom")}),1.0]])]});
            extrude(context, id + "F60", {"entities" : qUnion([Q0]), "depth" : 2000 * mm, "offsetDistance" : 25 * mm});
        }
        {
            var Q0;
            Q0=makeQuery(id+"F60.opExtrude","CAP_FACE",FACE,{"disambiguationData":[OSD([sQuery(id+"F59.wireOp",EDGE,"E50.bottom"),sQuery(id+"F59.wireOp",EDGE,"E50.top"),sQuery(id+"F59.wireOp",EDGE,"E50.left"),sQuery(id+"F59.wireOp",EDGE,"E50.right")])],"isStart":false});
            var sketch = newSketch(context, id + "F61", { "sketchPlane" : qUnion([Q0])});
            skLineSegment(sketch, "E51.bottom", {"start": v(-342.58, -641.93) * mm, "end": v(-362.58, -641.93) * mm});
            skLineSegment(sketch, "E51.top", {"start": v(-342.58, -661.93) * mm, "end": v(-362.58, -661.93) * mm});
            skLineSegment(sketch, "E51.left", {"start": v(-342.58, -641.93) * mm, "end": v(-342.58, -661.93) * mm});
            skLineSegment(sketch, "E51.right", {"start": v(-362.58, -641.93) * mm, "end": v(-362.58, -661.93) * mm});
            skPoint(sketch, "E51.middle", {"position": v(-352.58, -651.93) * mm});
            skSolve(sketch);
        }
        {
            var Q0;
            {var subQ0=sQuery(id+"F61.wireOp",EDGE,"E51.bottom");Q0=makeQuery(id+"F61.imprint","IMPRINT",FACE,{"disambiguationData":[TD([[makeQuery(id+"F61.imprint","IMPRINT",EDGE,{"derivedFrom":subQ0}),1.0]])]});}
            extrude(context, id + "F62", {"entities" : qUnion([Q0]), "operationType" : NewBodyOperationType.REMOVE, "oppositeDirection" : true, "depth" : 2000 * mm, "offsetDistance" : 25 * mm});
        }
        {
            var Q0;
            Q0=qCreatedBy(makeId("Top.planeOp"),FACE);
            var sketch = newSketch(context, id + "F63", { "sketchPlane" : qUnion([Q0])});
            skLineSegment(sketch, "E52.bottom", {"start": v(730.78, 0) * mm, "end": v(880.78, 0) * mm});
            skLineSegment(sketch, "E52.top", {"start": v(730.78, -60) * mm, "end": v(880.78, -60) * mm});
            skLineSegment(sketch, "E52.left", {"start": v(730.78, 0) * mm, "end": v(730.78, -60) * mm});
            skLineSegment(sketch, "E52.right", {"start": v(880.78, 0) * mm, "end": v(880.78, -60) * mm});
            skSolve(sketch);
        }
        {
            var Q0;
            Q0=makeQuery(id+"F63.imprint","IMPRINT",FACE,{"disambiguationData":[TD([[makeQuery(id+"F63.imprint","IMPRINT",EDGE,{"derivedFrom":sQuery(id+"F63.wireOp",EDGE,"E52.bottom")}),-1.0]])]});
            extrude(context, id + "F64", {"entities" : qUnion([Q0]), "depth" : 2300 * mm, "offsetDistance" : 25 * mm});
        }
        {
            var Q0;
            Q0=makeQuery(id+"F64.opExtrude","CAP_FACE",FACE,{"disambiguationData":[OSD([sQuery(id+"F63.wireOp",EDGE,"E52.bottom"),sQuery(id+"F63.wireOp",EDGE,"E52.top"),sQuery(id+"F63.wireOp",EDGE,"E52.left"),sQuery(id+"F63.wireOp",EDGE,"E52.right")])],"isStart":false});
            var sketch = newSketch(context, id + "F65", { "sketchPlane" : qUnion([Q0])});
            skLineSegment(sketch, "E53.bottom", {"start": v(815.78, -50) * mm, "end": v(795.78, -50) * mm});
            skLineSegment(sketch, "E53.top", {"start": v(815.78, -70) * mm, "end": v(795.78, -70) * mm});
            skLineSegment(sketch, "E53.left", {"start": v(815.78, -50) * mm, "end": v(815.78, -70) * mm});
            skLineSegment(sketch, "E53.right", {"start": v(795.78, -50) * mm, "end": v(795.78, -70) * mm});
            skPoint(sketch, "E53.middle", {"position": v(805.78, -60) * mm});
            skSolve(sketch);
        }
        {
            var Q0;
            {var subQ0=sQuery(id+"F65.wireOp",EDGE,"E53.bottom");Q0=makeQuery(id+"F65.imprint","IMPRINT",FACE,{"disambiguationData":[TD([[makeQuery(id+"F65.imprint","IMPRINT",EDGE,{"derivedFrom":subQ0}),1.0]])]});}
            extrude(context, id + "F66", {"entities" : qUnion([Q0]), "operationType" : NewBodyOperationType.REMOVE, "oppositeDirection" : true, "depth" : 2300 * mm, "offsetDistance" : 25 * mm, "hasSecondDirection" : true, "secondDirectionBound" : SecondDirectionBoundingType.THROUGH_ALL, "secondDirectionOppositeDirection" : false, "secondDirectionDepth" : 25 * mm});
        }
        {
            var Q0;
            Q0=qCreatedBy(makeId("Top.planeOp"),FACE);
            var sketch = newSketch(context, id + "F67", { "sketchPlane" : qUnion([Q0])});
            skCircle(sketch, "E54", {"center": v(-922.78, 998.34) * mm, "radius": 30 * mm});
            skSolve(sketch);
        }
        {
            var Q0;
            Q0=makeQuery(id+"F67.imprint","IMPRINT",FACE,{"disambiguationData":[TD([[makeQuery(id+"F67.imprint","IMPRINT",EDGE,{"derivedFrom":sQuery(id+"F67.wireOp",EDGE,"E54")}),1.0]])]});
            extrude(context, id + "F68", {"entities" : qUnion([Q0]), "depth" : 800 * mm, "offsetDistance" : 25 * mm});
        }
        {
            var Q0;
            Q0=qCreatedBy(makeId("Top.planeOp"),FACE);
            var sketch = newSketch(context, id + "F69", { "sketchPlane" : qUnion([Q0])});
            skLineSegment(sketch, "E55.bottom", {"start": v(-475.86, 808.07) * mm, "end": v(-541.86, 808.07) * mm});
            skLineSegment(sketch, "E55.top", {"start": v(-475.86, 2608.07) * mm, "end": v(-541.86, 2608.07) * mm});
            skLineSegment(sketch, "E55.left", {"start": v(-475.86, 808.07) * mm, "end": v(-475.86, 2608.07) * mm});
            skLineSegment(sketch, "E55.right", {"start": v(-541.86, 808.07) * mm, "end": v(-541.86, 2608.07) * mm});
            skCircle(sketch, "E56", {"center": v(-508.86, 808.07) * mm, "radius": 33 * mm});
            skCircle(sketch, "E57", {"center": v(-508.86, 2608.07) * mm, "radius": 33 * mm});
            skCircle(sketch, "E58", {"center": v(-508.86, 808.07) * mm, "radius": 30 * mm});
            skCircle(sketch, "E59", {"center": v(-508.86, 2608.07) * mm, "radius": 30 * mm});
            skLineSegment(sketch, "E60.bottom", {"start": v(-538.86, 2608.07) * mm, "end": v(-478.86, 2608.07) * mm});
            skLineSegment(sketch, "E60.top", {"start": v(-538.86, 808.07) * mm, "end": v(-478.86, 808.07) * mm});
            skLineSegment(sketch, "E60.left", {"start": v(-538.86, 2608.07) * mm, "end": v(-538.86, 808.07) * mm});
            skLineSegment(sketch, "E60.right", {"start": v(-478.86, 2608.07) * mm, "end": v(-478.86, 808.07) * mm});
            skSolve(sketch);
        }
        {
            var Q0;
            {var subQ0=sQuery(id+"F69.wireOp",EDGE,"E55.left");Q0=makeQuery(id+"F69.imprint","IMPRINT",FACE,{"disambiguationData":[TD([[makeQuery(id+"F69.imprint","IMPRINT",EDGE,{"derivedFrom":subQ0}),1.0]])]});}
            var Q1;
            {var subQ0=sQuery(id+"F69.wireOp",EDGE,"E55.right");Q1=makeQuery(id+"F69.imprint","IMPRINT",FACE,{"disambiguationData":[TD([[makeQuery(id+"F69.imprint","IMPRINT",EDGE,{"derivedFrom":subQ0}),-1.0]])]});}
            var Q2;
            {var subQ0=sQuery(id+"F69.wireOp",EDGE,"E56");var subQ1=sQuery(id+"F69.wireOp",EDGE,"E55.bottom");var subQ2=makeQuery(id+"F69.imprint","INTERSECT",VERTEX,{"derivedFrom":[subQ1,sQuery(id+"F69.wireOp",EDGE,"E55.left"),subQ0]});Q2=makeQuery(id+"F69.imprint","IMPRINT",FACE,{"disambiguationData":[TD([[makeQuery(id+"F69.imprint","IMPRINT",EDGE,{"disambiguationData":[TD([[subQ2,1.0]])],"derivedFrom":subQ0}),1.0]])]});}
            var Q3;
            {var subQ0=sQuery(id+"F69.wireOp",EDGE,"E56");var subQ3=sQuery(id+"F69.wireOp",EDGE,"E60.left");var subQ5=makeQuery(id+"F69.imprint","INTERSECT",VERTEX,{"derivedFrom":[subQ0,subQ3]});Q3=makeQuery(id+"F69.imprint","IMPRINT",FACE,{"disambiguationData":[TD([[makeQuery(id+"F69.imprint","IMPRINT",EDGE,{"disambiguationData":[TD([[subQ5,-1.0]])],"derivedFrom":subQ0}),1.0]])]});}
            var Q4;
            {var subQ0=sQuery(id+"F69.wireOp",EDGE,"E56");var subQ3=sQuery(id+"F69.wireOp",EDGE,"E60.right");var subQ5=makeQuery(id+"F69.imprint","INTERSECT",VERTEX,{"derivedFrom":[subQ0,subQ3]});Q4=makeQuery(id+"F69.imprint","IMPRINT",FACE,{"disambiguationData":[TD([[makeQuery(id+"F69.imprint","IMPRINT",EDGE,{"disambiguationData":[TD([[subQ5,1.0]])],"derivedFrom":subQ0}),1.0]])]});}
            var Q5;
            {var subQ0=sQuery(id+"F69.wireOp",EDGE,"E57");var subQ1=sQuery(id+"F69.wireOp",EDGE,"E55.top");var subQ2=makeQuery(id+"F69.imprint","INTERSECT",VERTEX,{"derivedFrom":[subQ1,sQuery(id+"F69.wireOp",EDGE,"E55.left"),subQ0]});Q5=makeQuery(id+"F69.imprint","IMPRINT",FACE,{"disambiguationData":[TD([[makeQuery(id+"F69.imprint","IMPRINT",EDGE,{"disambiguationData":[TD([[subQ2,-1.0]])],"derivedFrom":subQ0}),1.0]])]});}
            var Q6;
            {var subQ0=sQuery(id+"F69.wireOp",EDGE,"E57");var subQ3=sQuery(id+"F69.wireOp",EDGE,"E60.right");var subQ5=makeQuery(id+"F69.imprint","INTERSECT",VERTEX,{"derivedFrom":[subQ0,subQ3]});Q6=makeQuery(id+"F69.imprint","IMPRINT",FACE,{"disambiguationData":[TD([[makeQuery(id+"F69.imprint","IMPRINT",EDGE,{"disambiguationData":[TD([[subQ5,-1.0]])],"derivedFrom":subQ0}),1.0]])]});}
            var Q7;
            {var subQ0=sQuery(id+"F69.wireOp",EDGE,"E57");var subQ3=sQuery(id+"F69.wireOp",EDGE,"E60.left");var subQ5=makeQuery(id+"F69.imprint","INTERSECT",VERTEX,{"derivedFrom":[subQ0,subQ3]});Q7=makeQuery(id+"F69.imprint","IMPRINT",FACE,{"disambiguationData":[TD([[makeQuery(id+"F69.imprint","IMPRINT",EDGE,{"disambiguationData":[TD([[subQ5,1.0]])],"derivedFrom":subQ0}),1.0]])]});}
            extrude(context, id + "F70", {"entities" : qUnion([Q0, Q1, Q2, Q3, Q4, Q5, Q6, Q7]), "depth" : 800 * mm, "offsetDistance" : 25 * mm});
        }
        {
            var Q0;
            Q0=qCreatedBy(makeId("Top.planeOp"),FACE);
            var sketch = newSketch(context, id + "F71", { "sketchPlane" : qUnion([Q0])});
            skLineSegment(sketch, "E61.bottom", {"start": v(670.5, 2955.16) * mm, "end": v(1470.5, 2955.16) * mm});
            skLineSegment(sketch, "E61.top", {"start": v(670.5, 3555.16) * mm, "end": v(1470.5, 3555.16) * mm});
            skLineSegment(sketch, "E61.left", {"start": v(670.5, 2955.16) * mm, "end": v(670.5, 3555.16) * mm});
            skLineSegment(sketch, "E61.right", {"start": v(1470.5, 2955.16) * mm, "end": v(1470.5, 3555.16) * mm});
            skSolve(sketch);
        }
        {
            var Q0;
            Q0=makeQuery(id+"F71.imprint","IMPRINT",FACE,{"disambiguationData":[TD([[makeQuery(id+"F71.imprint","IMPRINT",EDGE,{"derivedFrom":sQuery(id+"F71.wireOp",EDGE,"E61.bottom")}),1.0]])]});
            extrude(context, id + "F72", {"entities" : qUnion([Q0]), "depth" : 5 * mm, "offsetDistance" : 25 * mm});
        }
        {
            var Q0;
            Q0=qCreatedBy(makeId("Top.planeOp"),FACE);
            var sketch = newSketch(context, id + "F73", { "sketchPlane" : qUnion([Q0])});
            skLineSegment(sketch, "E62.bottom", {"start": v(1519.39, 2775.24) * mm, "end": v(1419.39, 2775.24) * mm});
            skLineSegment(sketch, "E62.top", {"start": v(1519.39, 2835.24) * mm, "end": v(1419.39, 2835.24) * mm});
            skLineSegment(sketch, "E62.left", {"start": v(1519.39, 2775.24) * mm, "end": v(1519.39, 2835.24) * mm});
            skLineSegment(sketch, "E62.right", {"start": v(1419.39, 2775.24) * mm, "end": v(1419.39, 2835.24) * mm});
            skSolve(sketch);
        }
        {
            var Q0;
            Q0=makeQuery(id+"F73.imprint","IMPRINT",FACE,{"disambiguationData":[TD([[makeQuery(id+"F73.imprint","IMPRINT",EDGE,{"derivedFrom":sQuery(id+"F73.wireOp",EDGE,"E62.bottom")}),-1.0]])]});
            extrude(context, id + "F74", {"entities" : qUnion([Q0]), "depth" : 40 * mm, "offsetDistance" : 25 * mm});
        }
        {
            var Q0;
            Q0=qCreatedBy(makeId("Top.planeOp"),FACE);
            var sketch = newSketch(context, id + "F75", { "sketchPlane" : qUnion([Q0])});
            skLineSegment(sketch, "E63.bottom", {"start": v(1932.85, 3207.65) * mm, "end": v(2232.85, 3207.65) * mm});
            skLineSegment(sketch, "E63.top", {"start": v(1932.85, 3607.65) * mm, "end": v(2232.85, 3607.65) * mm});
            skLineSegment(sketch, "E63.left", {"start": v(1932.85, 3207.65) * mm, "end": v(1932.85, 3607.65) * mm});
            skLineSegment(sketch, "E63.right", {"start": v(2232.85, 3207.65) * mm, "end": v(2232.85, 3607.65) * mm});
            skSolve(sketch);
        }
        {
            var Q0;
            Q0=makeQuery(id+"F75.imprint","IMPRINT",FACE,{"disambiguationData":[TD([[makeQuery(id+"F75.imprint","IMPRINT",EDGE,{"derivedFrom":sQuery(id+"F75.wireOp",EDGE,"E63.bottom")}),1.0]])]});
            extrude(context, id + "F76", {"entities" : qUnion([Q0]), "depth" : 70 * mm, "offsetDistance" : 25 * mm});
        }
    });
